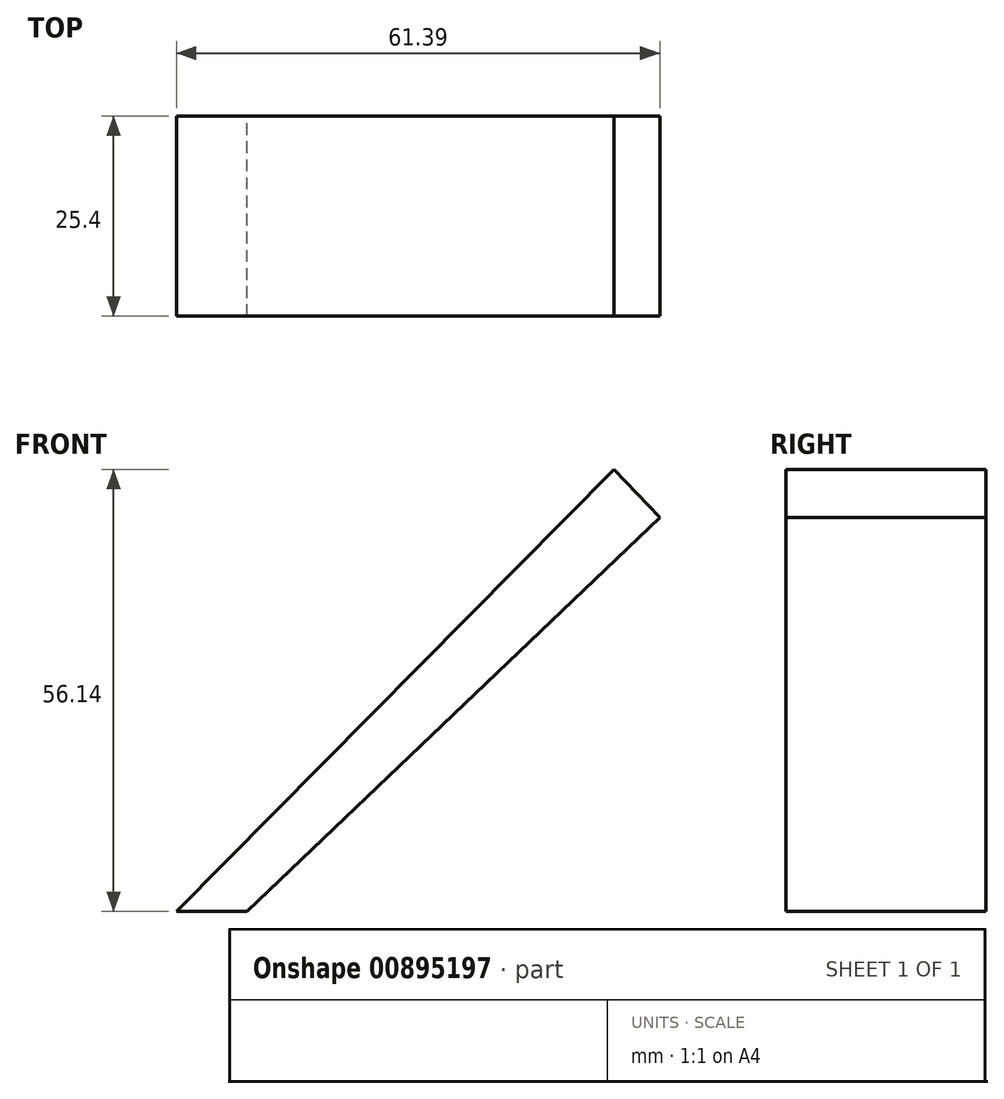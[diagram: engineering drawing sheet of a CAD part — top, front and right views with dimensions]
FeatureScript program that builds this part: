
annotation { "Feature Type Name" : "Feature", "Feature Type Description" : "" }
export const myFeature = defineFeature(function(context is Context, id is Id, definition is map)
    precondition{}
    {
        {
            var Q0;
            Q0=qCreatedBy(makeId("Front.planeOp"),FACE);
            var sketch = newSketch(context, id + "F0", { "sketchPlane" : qUnion([Q0])});
            skLineSegment(sketch, "E0", {"start": v(-55.58, 0) * mm, "end": v(0, 56.14) * mm});
            skLineSegment(sketch, "E1", {"start": v(0, 56.14) * mm, "end": v(5.8, 50.05) * mm});
            skLineSegment(sketch, "E2", {"start": v(5.8, 50.05) * mm, "end": v(-46.6, 0) * mm});
            skLineSegment(sketch, "E3", {"start": v(-46.6, 0) * mm, "end": v(-55.58, 0) * mm});
            skSolve(sketch);
        }
        {
            var Q0;
            Q0=makeQuery(id+"F0.imprint","IMPRINT",FACE,{"disambiguationData":[TD([[makeQuery(id+"F0.imprint","IMPRINT",EDGE,{"derivedFrom":sQuery(id+"F0.wireOp",EDGE,"E0")}),-1.0]])]});
            extrude(context, id + "F1", {"entities" : qUnion([Q0]), "depth" : 25.4 * mm, "offsetDistance" : 25.4 * mm});
        }
    });
